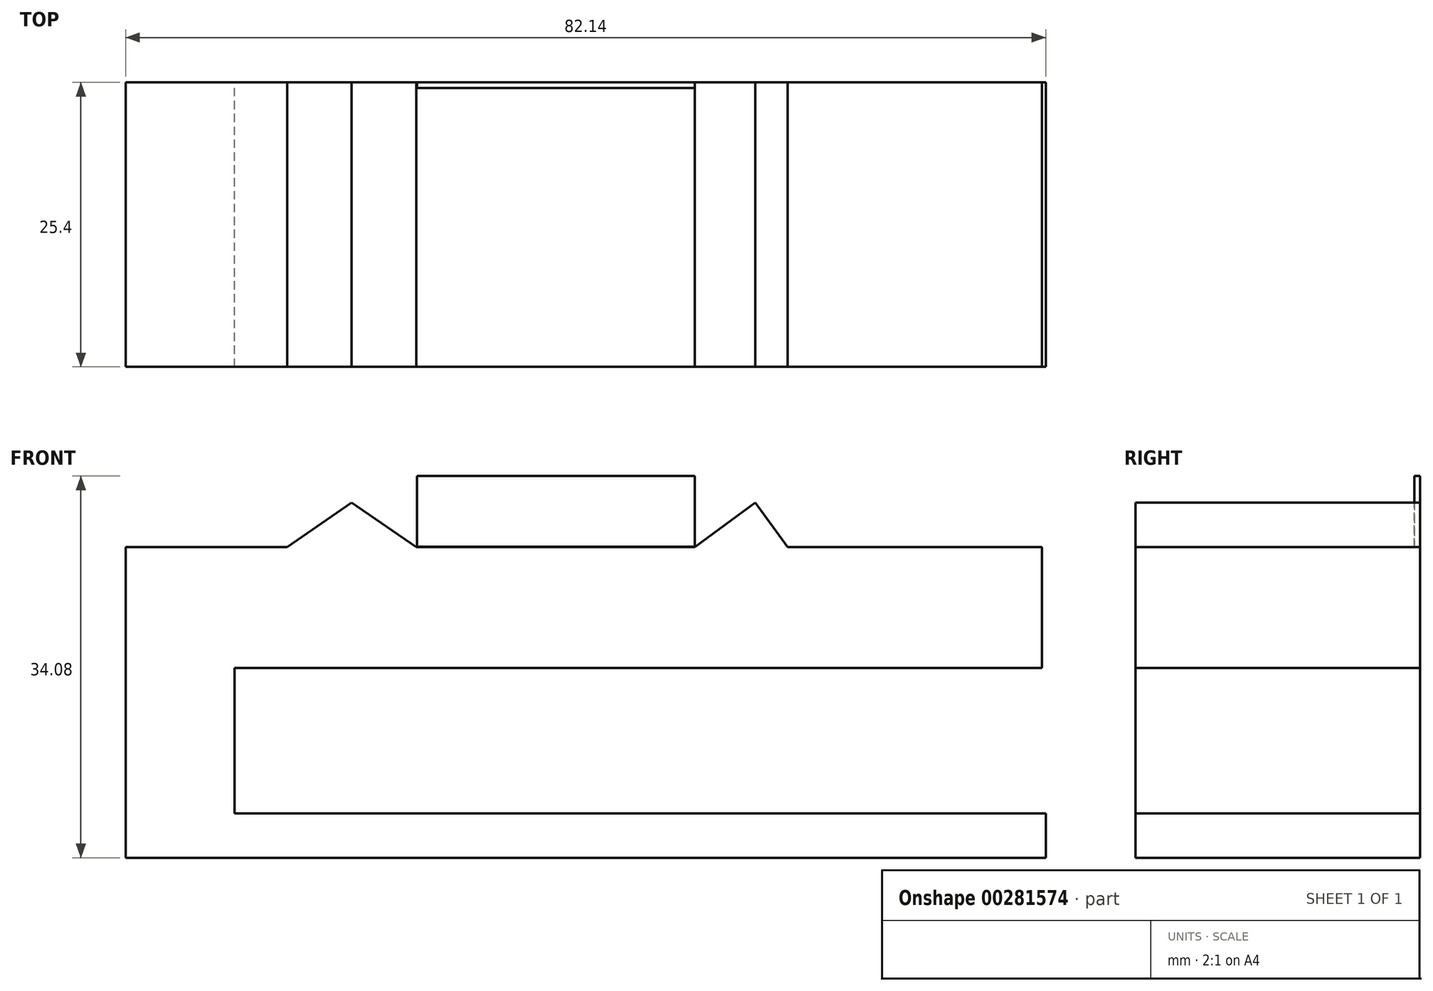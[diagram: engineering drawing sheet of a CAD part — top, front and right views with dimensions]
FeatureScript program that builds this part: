
annotation { "Feature Type Name" : "Feature", "Feature Type Description" : "" }
export const myFeature = defineFeature(function(context is Context, id is Id, definition is map)
    precondition{}
    {
        {
            var Q0;
            Q0=qCreatedBy(makeId("Front.planeOp"),FACE);
            var sketch = newSketch(context, id + "F0", { "sketchPlane" : qUnion([Q0])});
            skLineSegment(sketch, "E0.bottom", {"start": v(-41.07, 0) * mm, "end": v(41.07, 0) * mm});
            skLineSegment(sketch, "E0.top", {"start": v(-41.07, 0) * mm, "end": v(41.07, 0) * mm});
            skLineSegment(sketch, "E0.left", {"start": v(-41.07, 0) * mm, "end": v(-41.07, 0) * mm});
            skLineSegment(sketch, "E0.right", {"start": v(41.07, 0) * mm, "end": v(41.07, 0) * mm});
            skPoint(sketch, "E0.middle", {"position": v(0, 0) * mm});
            skLineSegment(sketch, "E1", {"start": v(-41.07, 0) * mm, "end": v(-41.07, 27.74) * mm});
            skLineSegment(sketch, "E2", {"start": v(-41.07, 27.74) * mm, "end": v(40.71, 27.74) * mm});
            skLineSegment(sketch, "E3", {"start": v(40.71, 27.74) * mm, "end": v(40.71, 16.93) * mm});
            skLineSegment(sketch, "E4", {"start": v(40.71, 16.93) * mm, "end": v(-31.34, 16.93) * mm});
            skLineSegment(sketch, "E5", {"start": v(-31.34, 16.93) * mm, "end": v(-31.34, 3.96) * mm});
            skLineSegment(sketch, "E6", {"start": v(-31.34, 3.96) * mm, "end": v(41.07, 3.96) * mm});
            skLineSegment(sketch, "E7", {"start": v(41.07, 3.96) * mm, "end": v(41.07, 0) * mm});
            skLineSegment(sketch, "E8", {"start": v(-15.13, 27.74) * mm, "end": v(-20.9, 31.7) * mm});
            skLineSegment(sketch, "E9", {"start": v(-20.9, 31.7) * mm, "end": v(-26.66, 27.74) * mm});
            skLineSegment(sketch, "E10", {"start": v(9.73, 27.74) * mm, "end": v(15.13, 31.7) * mm});
            skLineSegment(sketch, "E11", {"start": v(15.13, 31.7) * mm, "end": v(18.04, 27.74) * mm});
            skSolve(sketch);
        }
        {
            var Q0;
            Q0 = qSketchRegion(id + "F0", true);
            extrude(context, id + "F1", {"entities" : qUnion([Q0]), "depth" : 25.4 * mm});
        }
        {
            var Q0;
            Q0=qCreatedBy(makeId("Front.planeOp"),FACE);
            var sketch = newSketch(context, id + "F2", { "sketchPlane" : qUnion([Q0])});
            skLineSegment(sketch, "E12", {"start": v(9.72, 27.77) * mm, "end": v(9.72, 34.08) * mm});
            skLineSegment(sketch, "E13", {"start": v(9.72, 34.08) * mm, "end": v(-15.05, 34.08) * mm});
            skLineSegment(sketch, "E14", {"start": v(-15.05, 34.08) * mm, "end": v(-15.05, 27.77) * mm});
            skLineSegment(sketch, "E15", {"start": v(-15.05, 27.77) * mm, "end": v(9.72, 27.77) * mm});
            skSolve(sketch);
        }
        {
            var Q0;
            Q0 = qSketchRegion(id + "F2", true);
            extrude(context, id + "F3", {"entities" : qUnion([Q0]), "depth" : 0.5 * mm});
        }
    });
